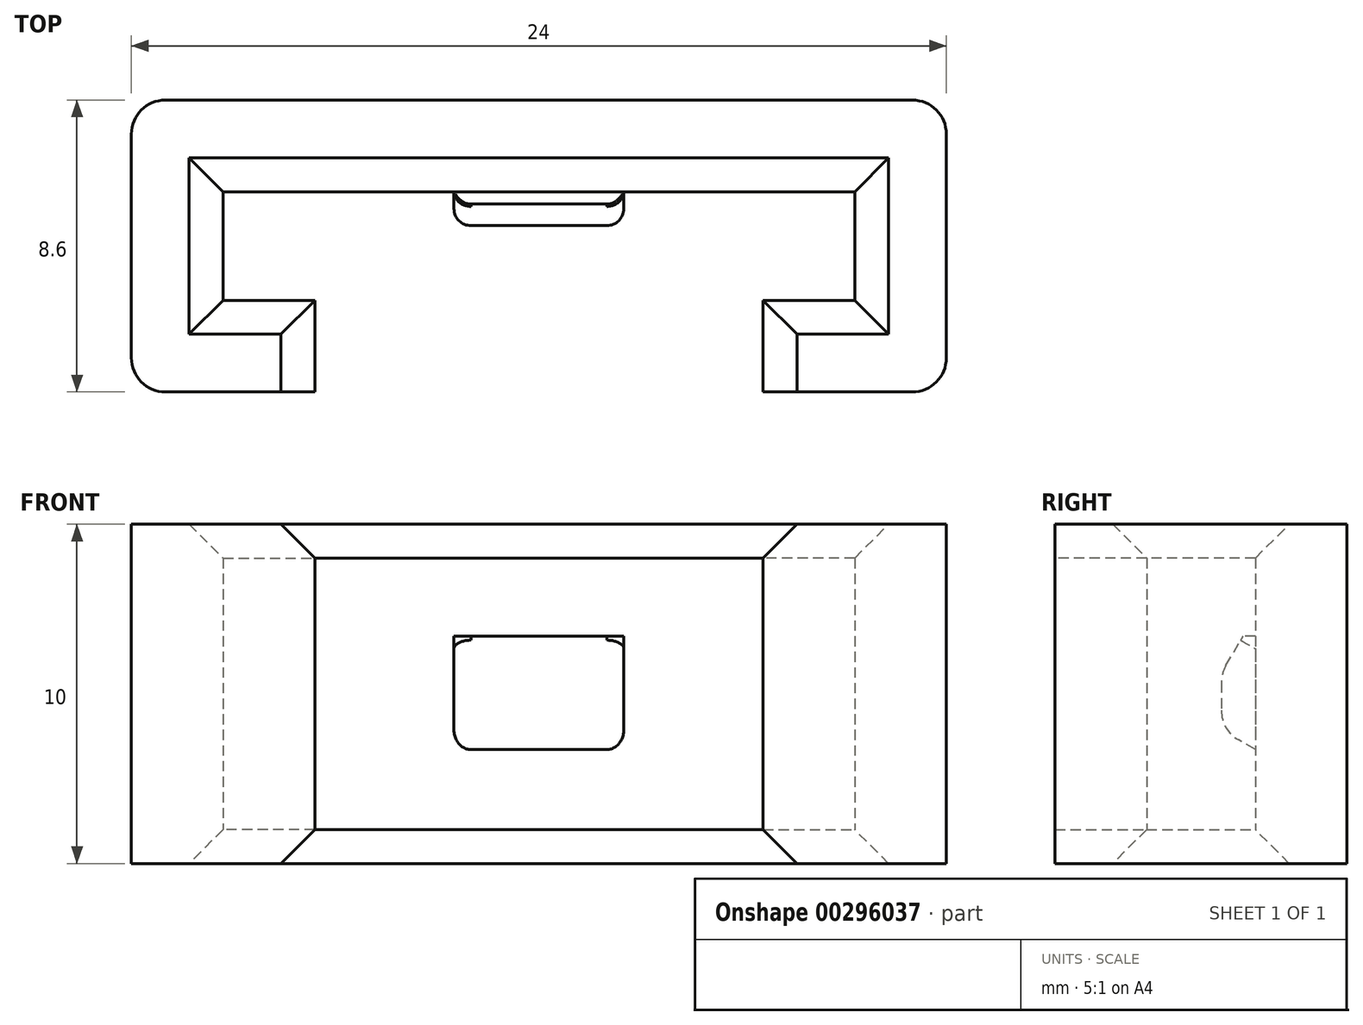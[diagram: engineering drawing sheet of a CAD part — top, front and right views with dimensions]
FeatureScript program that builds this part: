
annotation { "Feature Type Name" : "Feature", "Feature Type Description" : "" }
export const myFeature = defineFeature(function(context is Context, id is Id, definition is map)
    precondition{}
    {
        {
            var Q0;
            Q0=qCreatedBy(makeId("Top.planeOp"),FACE);
            var sketch = newSketch(context, id + "F0", { "sketchPlane" : qUnion([Q0])});
            skLineSegment(sketch, "E0", {"start": v(0, -17.47) * mm, "end": v(0, 25.01) * mm, "construction": true});
            skLineSegment(sketch, "E1", {"start": v(-9.3, -5.9) * mm, "end": v(-6.6, -5.9) * mm});
            skLineSegment(sketch, "E2", {"start": v(-6.6, -5.9) * mm, "end": v(-6.6, -8.6) * mm});
            skLineSegment(sketch, "E3", {"start": v(-6.6, -8.6) * mm, "end": v(-12, -8.6) * mm});
            skLineSegment(sketch, "E4", {"start": v(-12, -8.6) * mm, "end": v(-12, 0) * mm});
            skLineSegment(sketch, "E5", {"start": v(-12, 0) * mm, "end": v(0, 0) * mm});
            skLineSegment(sketch, "E6", {"start": v(-9.3, -5.9) * mm, "end": v(-9.3, -2.7) * mm});
            skLineSegment(sketch, "E7", {"start": v(-9.3, -2.7) * mm, "end": v(0, -2.7) * mm});
            skLineSegment(sketch, "E8.MirrorCS", {"start": v(9.3, -5.9) * mm, "end": v(6.6, -5.9) * mm});
            skLineSegment(sketch, "E9.MirrorCS", {"start": v(9.3, -5.9) * mm, "end": v(9.3, -2.7) * mm});
            skLineSegment(sketch, "E10.MirrorCS", {"start": v(6.6, -5.9) * mm, "end": v(6.6, -8.6) * mm});
            skLineSegment(sketch, "E11.MirrorCS", {"start": v(12, -8.6) * mm, "end": v(12, 0) * mm});
            skLineSegment(sketch, "E12.MirrorCS", {"start": v(6.6, -8.6) * mm, "end": v(12, -8.6) * mm});
            skLineSegment(sketch, "E13.MirrorCS", {"start": v(12, 0) * mm, "end": v(0, 0) * mm});
            skLineSegment(sketch, "E14.MirrorCS", {"start": v(9.3, -2.7) * mm, "end": v(0, -2.7) * mm});
            skSolve(sketch);
        }
        {
            var Q0;
            Q0 = qSketchRegion(id + "F0", true);
            extrude(context, id + "F1", {"entities" : qUnion([Q0]), "depth" : 10 * mm});
        }
        {
            var Q0;
            Q0=makeQuery(id+"F1.opExtrude","SWEPT_FACE",FACE,{"disambiguationData":[OSD([sQuery(id+"F0.wireOp",EDGE,"E7"),sQuery(id+"F0.wireOp",EDGE,"E14.MirrorCS")])]});
            var sketch = newSketch(context, id + "F2", { "sketchPlane" : qUnion([Q0])});
            skLineSegment(sketch, "E15", {"start": v(0, 0) * mm, "end": v(0, 10) * mm, "construction": true});
            skLineSegment(sketch, "E16.bottom", {"start": v(2.5, 6.7) * mm, "end": v(-2.5, 6.7) * mm});
            skLineSegment(sketch, "E16.top", {"start": v(2.5, 3.3) * mm, "end": v(-2.5, 3.3) * mm});
            skLineSegment(sketch, "E16.left", {"start": v(2.5, 6.7) * mm, "end": v(2.5, 3.3) * mm});
            skLineSegment(sketch, "E16.right", {"start": v(-2.5, 6.7) * mm, "end": v(-2.5, 3.3) * mm});
            skPoint(sketch, "E16.middle", {"position": v(0, 5) * mm});
            skSolve(sketch);
        }
        {
            var Q0;
            Q0 = qSketchRegion(id + "F2", true);
            extrude(context, id + "F3", {"entities" : qUnion([Q0]), "operationType" : NewBodyOperationType.ADD, "depth" : 1 * mm});
        }
        {
            var Q0;
            Q0=makeQuery(id+"F3.opExtrude","CAP_EDGE",EDGE,{"disambiguationData":[OSD([sQuery(id+"F2.wireOp",EDGE,"E16.bottom")])],"isStart":false});
            var Q1;
            Q1=makeQuery(id+"F3.opExtrude","CAP_EDGE",EDGE,{"disambiguationData":[OSD([sQuery(id+"F2.wireOp",EDGE,"E16.top")])],"isStart":false});
            chamfer(context, id + "F4", {"entities" : qUnion([Q0, Q1]), "chamferType" : ChamferType.OFFSET_ANGLE, "width" : 1.1 * mm, "oppositeDirection" : true, "angle" : 30 * degree, "tangentPropagation" : true});
        }
        {
            var Q0;
            {var subQ0=sQuery(id+"F2.wireOp",EDGE,"E16.top");Q0=makeQuery(id+"F4.opChamfer","BLEND_EDGE",EDGE,{"blendedFrom":[makeQuery(id+"F3.opExtrude","CAP_EDGE",EDGE,{"disambiguationData":[OSD([subQ0])],"isStart":false}),makeQuery(id+"F3.opExtrude","CAP_FACE",FACE,{"disambiguationData":[OSD([sQuery(id+"F2.wireOp",EDGE,"E16.bottom"),subQ0,sQuery(id+"F2.wireOp",EDGE,"E16.left"),sQuery(id+"F2.wireOp",EDGE,"E16.right")])],"isStart":false})],"blendedInto":[makeQuery(id+"F3.opExtrude","CAP_FACE",FACE,{"disambiguationData":[OSD([sQuery(id+"F2.wireOp",EDGE,"E16.bottom"),subQ0,sQuery(id+"F2.wireOp",EDGE,"E16.left"),sQuery(id+"F2.wireOp",EDGE,"E16.right")])],"isStart":false})]});}
            var Q1;
            {var subQ0=sQuery(id+"F2.wireOp",EDGE,"E16.bottom");Q1=makeQuery(id+"F4.opChamfer","BLEND_EDGE",EDGE,{"blendedFrom":[makeQuery(id+"F3.opExtrude","CAP_EDGE",EDGE,{"disambiguationData":[OSD([subQ0])],"isStart":false}),makeQuery(id+"F3.opExtrude","CAP_FACE",FACE,{"disambiguationData":[OSD([subQ0,sQuery(id+"F2.wireOp",EDGE,"E16.top"),sQuery(id+"F2.wireOp",EDGE,"E16.left"),sQuery(id+"F2.wireOp",EDGE,"E16.right")])],"isStart":false})],"blendedInto":[makeQuery(id+"F3.opExtrude","CAP_FACE",FACE,{"disambiguationData":[OSD([subQ0,sQuery(id+"F2.wireOp",EDGE,"E16.top"),sQuery(id+"F2.wireOp",EDGE,"E16.left"),sQuery(id+"F2.wireOp",EDGE,"E16.right")])],"isStart":false})]});}
            fillet(context, id + "F5", {"entities" : qUnion([Q0, Q1]), "radius" : 1 * mm, "tangentPropagation" : true, "allowEdgeOverflow" : false});
        }
        {
            var Q0;
            {var subQ0=sQuery(id+"F2.wireOp",EDGE,"E16.left");var subQ1=sQuery(id+"F2.wireOp",EDGE,"E16.top");Q0=makeQuery(id+"F5.opFillet","BLEND_EDGE",EDGE,{"blendedFrom":[makeQuery(id+"F4.opChamfer","BLEND_EDGE",EDGE,{"blendedFrom":[makeQuery(id+"F3.opExtrude","CAP_EDGE",EDGE,{"disambiguationData":[OSD([subQ1])],"isStart":false}),makeQuery(id+"F3.opExtrude","CAP_FACE",FACE,{"disambiguationData":[OSD([sQuery(id+"F2.wireOp",EDGE,"E16.bottom"),subQ1,subQ0,sQuery(id+"F2.wireOp",EDGE,"E16.right")])],"isStart":false})],"blendedInto":[makeQuery(id+"F3.opExtrude","CAP_FACE",FACE,{"disambiguationData":[OSD([sQuery(id+"F2.wireOp",EDGE,"E16.bottom"),subQ1,subQ0,sQuery(id+"F2.wireOp",EDGE,"E16.right")])],"isStart":false})]}),makeQuery(id+"F3.opExtrude","SWEPT_FACE",FACE,{"disambiguationData":[OSD([subQ0])]})],"blendedInto":[makeQuery(id+"F3.opExtrude","SWEPT_FACE",FACE,{"disambiguationData":[OSD([subQ0])]})]});}
            var Q1;
            {var subQ0=sQuery(id+"F2.wireOp",EDGE,"E16.left");var subQ1=sQuery(id+"F2.wireOp",EDGE,"E16.bottom");Q1=makeQuery(id+"F5.opFillet","BLEND_EDGE",EDGE,{"blendedFrom":[makeQuery(id+"F4.opChamfer","BLEND_EDGE",EDGE,{"blendedFrom":[makeQuery(id+"F3.opExtrude","CAP_EDGE",EDGE,{"disambiguationData":[OSD([subQ1])],"isStart":false}),makeQuery(id+"F3.opExtrude","CAP_FACE",FACE,{"disambiguationData":[OSD([subQ1,sQuery(id+"F2.wireOp",EDGE,"E16.top"),subQ0,sQuery(id+"F2.wireOp",EDGE,"E16.right")])],"isStart":false})],"blendedInto":[makeQuery(id+"F3.opExtrude","CAP_FACE",FACE,{"disambiguationData":[OSD([subQ1,sQuery(id+"F2.wireOp",EDGE,"E16.top"),subQ0,sQuery(id+"F2.wireOp",EDGE,"E16.right")])],"isStart":false})]}),makeQuery(id+"F3.opExtrude","SWEPT_FACE",FACE,{"disambiguationData":[OSD([subQ0])]})],"blendedInto":[makeQuery(id+"F3.opExtrude","SWEPT_FACE",FACE,{"disambiguationData":[OSD([subQ0])]})]});}
            var Q2;
            {var subQ0=sQuery(id+"F2.wireOp",EDGE,"E16.right");var subQ1=sQuery(id+"F2.wireOp",EDGE,"E16.top");Q2=makeQuery(id+"F5.opFillet","BLEND_EDGE",EDGE,{"blendedFrom":[makeQuery(id+"F4.opChamfer","BLEND_EDGE",EDGE,{"blendedFrom":[makeQuery(id+"F3.opExtrude","CAP_EDGE",EDGE,{"disambiguationData":[OSD([subQ1])],"isStart":false}),makeQuery(id+"F3.opExtrude","CAP_FACE",FACE,{"disambiguationData":[OSD([sQuery(id+"F2.wireOp",EDGE,"E16.bottom"),subQ1,sQuery(id+"F2.wireOp",EDGE,"E16.left"),subQ0])],"isStart":false})],"blendedInto":[makeQuery(id+"F3.opExtrude","CAP_FACE",FACE,{"disambiguationData":[OSD([sQuery(id+"F2.wireOp",EDGE,"E16.bottom"),subQ1,sQuery(id+"F2.wireOp",EDGE,"E16.left"),subQ0])],"isStart":false})]}),makeQuery(id+"F3.opExtrude","SWEPT_FACE",FACE,{"disambiguationData":[OSD([subQ0])]})],"blendedInto":[makeQuery(id+"F3.opExtrude","SWEPT_FACE",FACE,{"disambiguationData":[OSD([subQ0])]})]});}
            var Q3;
            {var subQ0=sQuery(id+"F2.wireOp",EDGE,"E16.right");var subQ1=sQuery(id+"F2.wireOp",EDGE,"E16.bottom");Q3=makeQuery(id+"F5.opFillet","BLEND_EDGE",EDGE,{"blendedFrom":[makeQuery(id+"F4.opChamfer","BLEND_EDGE",EDGE,{"blendedFrom":[makeQuery(id+"F3.opExtrude","CAP_EDGE",EDGE,{"disambiguationData":[OSD([subQ1])],"isStart":false}),makeQuery(id+"F3.opExtrude","CAP_FACE",FACE,{"disambiguationData":[OSD([subQ1,sQuery(id+"F2.wireOp",EDGE,"E16.top"),sQuery(id+"F2.wireOp",EDGE,"E16.left"),subQ0])],"isStart":false})],"blendedInto":[makeQuery(id+"F3.opExtrude","CAP_FACE",FACE,{"disambiguationData":[OSD([subQ1,sQuery(id+"F2.wireOp",EDGE,"E16.top"),sQuery(id+"F2.wireOp",EDGE,"E16.left"),subQ0])],"isStart":false})]}),makeQuery(id+"F3.opExtrude","SWEPT_FACE",FACE,{"disambiguationData":[OSD([subQ0])]})],"blendedInto":[makeQuery(id+"F3.opExtrude","SWEPT_FACE",FACE,{"disambiguationData":[OSD([subQ0])]})]});}
            fillet(context, id + "F6", {"entities" : qUnion([Q0, Q1, Q2, Q3]), "radius" : 0.5 * mm, "tangentPropagation" : true, "allowEdgeOverflow" : false});
        }
        {
            var Q0;
            Q0=makeQuery(id+"F1.opExtrude","CAP_EDGE",EDGE,{"disambiguationData":[OSD([sQuery(id+"F0.wireOp",EDGE,"E6")])],"isStart":true});
            var Q1;
            Q1=makeQuery(id+"F1.opExtrude","CAP_EDGE",EDGE,{"disambiguationData":[OSD([sQuery(id+"F0.wireOp",EDGE,"E7"),sQuery(id+"F0.wireOp",EDGE,"E14.MirrorCS")])],"isStart":true});
            var Q2;
            Q2=makeQuery(id+"F1.opExtrude","CAP_EDGE",EDGE,{"disambiguationData":[OSD([sQuery(id+"F0.wireOp",EDGE,"E1")])],"isStart":true});
            var Q3;
            Q3=makeQuery(id+"F1.opExtrude","CAP_EDGE",EDGE,{"disambiguationData":[OSD([sQuery(id+"F0.wireOp",EDGE,"E2")])],"isStart":true});
            var Q4;
            Q4=makeQuery(id+"F1.opExtrude","CAP_EDGE",EDGE,{"disambiguationData":[OSD([sQuery(id+"F0.wireOp",EDGE,"E9.MirrorCS")])],"isStart":true});
            var Q5;
            Q5=makeQuery(id+"F1.opExtrude","CAP_EDGE",EDGE,{"disambiguationData":[OSD([sQuery(id+"F0.wireOp",EDGE,"E8.MirrorCS")])],"isStart":true});
            var Q6;
            Q6=makeQuery(id+"F1.opExtrude","CAP_EDGE",EDGE,{"disambiguationData":[OSD([sQuery(id+"F0.wireOp",EDGE,"E10.MirrorCS")])],"isStart":true});
            var Q7;
            Q7=makeQuery(id+"F1.opExtrude","CAP_EDGE",EDGE,{"disambiguationData":[OSD([sQuery(id+"F0.wireOp",EDGE,"E6")])],"isStart":false});
            var Q8;
            Q8=makeQuery(id+"F1.opExtrude","CAP_EDGE",EDGE,{"disambiguationData":[OSD([sQuery(id+"F0.wireOp",EDGE,"E1")])],"isStart":false});
            var Q9;
            Q9=makeQuery(id+"F1.opExtrude","CAP_EDGE",EDGE,{"disambiguationData":[OSD([sQuery(id+"F0.wireOp",EDGE,"E2")])],"isStart":false});
            var Q10;
            Q10=makeQuery(id+"F1.opExtrude","CAP_EDGE",EDGE,{"disambiguationData":[OSD([sQuery(id+"F0.wireOp",EDGE,"E7"),sQuery(id+"F0.wireOp",EDGE,"E14.MirrorCS")])],"isStart":false});
            var Q11;
            Q11=makeQuery(id+"F1.opExtrude","CAP_EDGE",EDGE,{"disambiguationData":[OSD([sQuery(id+"F0.wireOp",EDGE,"E9.MirrorCS")])],"isStart":false});
            var Q12;
            Q12=makeQuery(id+"F1.opExtrude","CAP_EDGE",EDGE,{"disambiguationData":[OSD([sQuery(id+"F0.wireOp",EDGE,"E8.MirrorCS")])],"isStart":false});
            var Q13;
            Q13=makeQuery(id+"F1.opExtrude","CAP_EDGE",EDGE,{"disambiguationData":[OSD([sQuery(id+"F0.wireOp",EDGE,"E10.MirrorCS")])],"isStart":false});
            chamfer(context, id + "F7", {"entities" : qUnion([Q0, Q1, Q2, Q3, Q4, Q5, Q6, Q7, Q8, Q9, Q10, Q11, Q12, Q13]), "width" : 1 * mm, "tangentPropagation" : true});
        }
        {
            var Q0;
            Q0=makeQuery(id+"F1.opExtrude","SWEPT_EDGE",EDGE,{"disambiguationData":[OSD([sQuery(id+"F0.wireOp",EDGE,"E3"),sQuery(id+"F0.wireOp",EDGE,"E4")])]});
            var Q1;
            Q1=makeQuery(id+"F1.opExtrude","SWEPT_EDGE",EDGE,{"disambiguationData":[OSD([sQuery(id+"F0.wireOp",EDGE,"E11.MirrorCS"),sQuery(id+"F0.wireOp",EDGE,"E12.MirrorCS")])]});
            var Q2;
            Q2=makeQuery(id+"F1.opExtrude","SWEPT_EDGE",EDGE,{"disambiguationData":[OSD([sQuery(id+"F0.wireOp",EDGE,"E4"),sQuery(id+"F0.wireOp",EDGE,"E5")])]});
            var Q3;
            Q3=makeQuery(id+"F1.opExtrude","SWEPT_EDGE",EDGE,{"disambiguationData":[OSD([sQuery(id+"F0.wireOp",EDGE,"E11.MirrorCS"),sQuery(id+"F0.wireOp",EDGE,"E13.MirrorCS")])]});
            fillet(context, id + "F8", {"entities" : qUnion([Q0, Q1, Q2, Q3]), "radius" : 1 * mm, "tangentPropagation" : true, "allowEdgeOverflow" : false});
        }
    });
